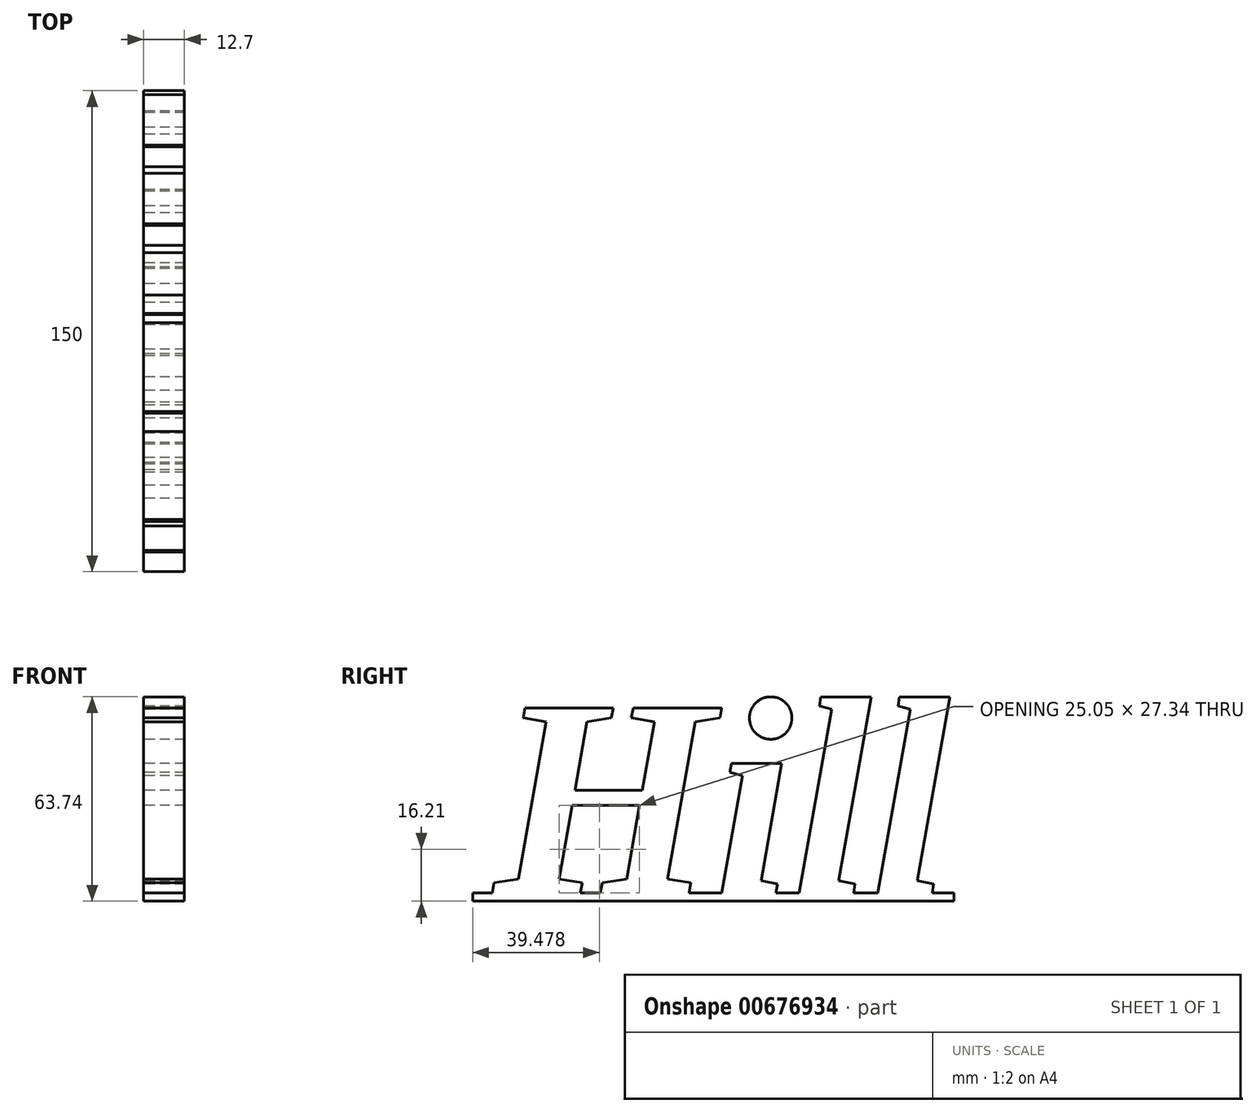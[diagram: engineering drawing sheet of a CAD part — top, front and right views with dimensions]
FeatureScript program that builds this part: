
annotation { "Feature Type Name" : "Feature", "Feature Type Description" : "" }
export const myFeature = defineFeature(function(context is Context, id is Id, definition is map)
    precondition{}
    {
        {
            var Q0;
            Q0=qCreatedBy(makeId("Right.planeOp"),FACE);
            var sketch = newSketch(context, id + "F0", { "sketchPlane" : qUnion([Q0])});
            skLineSegment(sketch, "E0.bottom", {"start": v(69.6, -2.54) * mm, "end": v(-80.4, -2.54) * mm});
            skLineSegment(sketch, "E0.top", {"start": v(69.6, 0) * mm, "end": v(-80.4, 0) * mm});
            skLineSegment(sketch, "E0.left", {"start": v(69.6, -2.54) * mm, "end": v(69.6, 0) * mm});
            skLineSegment(sketch, "E0.right", {"start": v(-80.4, -2.54) * mm, "end": v(-80.4, 0) * mm});
            skSolve(sketch);
        }
        {
            var Q0;
            Q0=qSketchRegion(id+"F0",true);
            extrude(context, id + "F1", {"entities" : qUnion([Q0]), "endBound" : BoundingType.SYMMETRIC, "oppositeDirection" : true, "depth" : 12.7 * mm, "offsetDistance" : 25.4 * mm});
        }
        {
            var Q0;
            Q0=qCreatedBy(makeId("Right.planeOp"),FACE);
            var sketch = newSketch(context, id + "F2", { "sketchPlane" : qUnion([Q0])});
            skText(sketch, "E1", { "text": "Hill", "fontName": "Tinos-BoldItalic.ttf"});
            const initialGuessF2  = {"E1": [-0.07364, 0, 1, 0, 0.0635]};
            skSetInitialGuess(sketch, initialGuessF2);
            skSolve(sketch);
        }
        {
            var Q0;
            Q0=qSketchRegion(id+"F2",true);
            extrude(context, id + "F3", {"entities" : qUnion([Q0]), "operationType" : NewBodyOperationType.ADD, "endBound" : BoundingType.SYMMETRIC, "depth" : 12.7 * mm, "offsetDistance" : 25.4 * mm});
        }
    });
